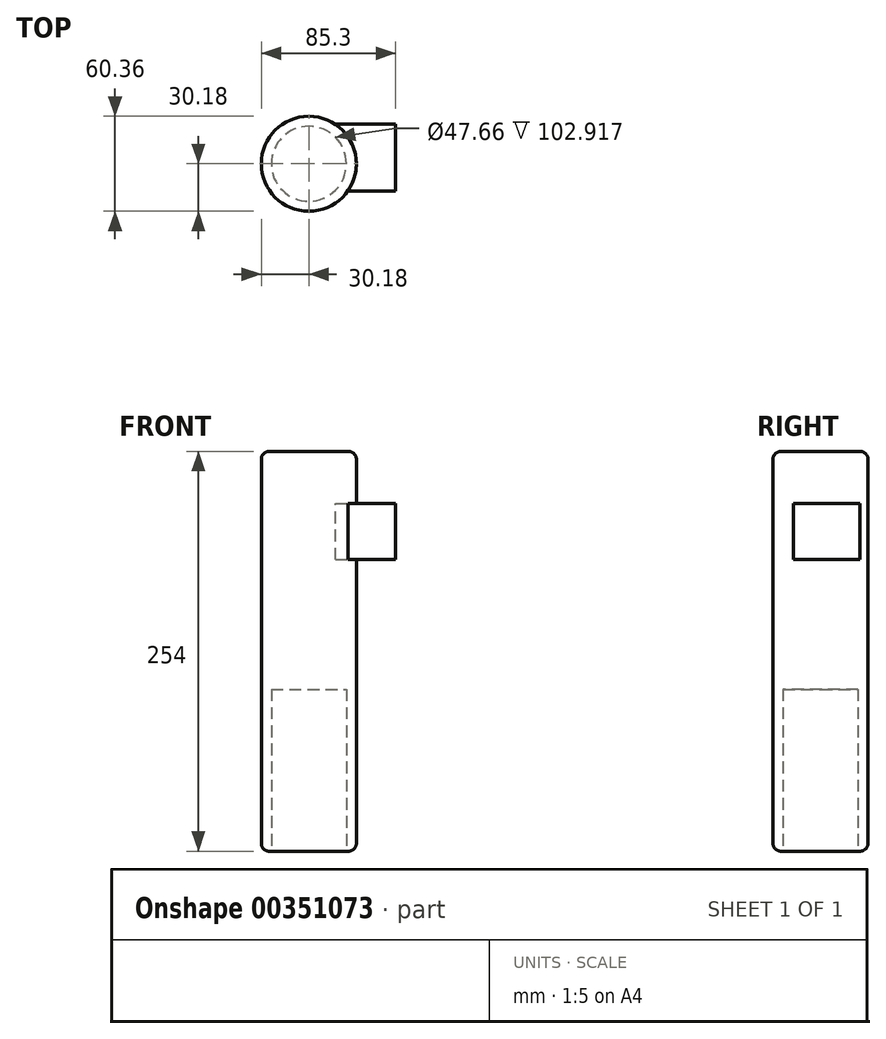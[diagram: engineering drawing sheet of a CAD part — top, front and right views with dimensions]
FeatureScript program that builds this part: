
annotation { "Feature Type Name" : "Feature", "Feature Type Description" : "" }
export const myFeature = defineFeature(function(context is Context, id is Id, definition is map)
    precondition{}
    {
        {
            var Q0;
            Q0=qCreatedBy(makeId("Top.planeOp"),FACE);
            var sketch = newSketch(context, id + "F0", { "sketchPlane" : qUnion([Q0])});
            skCircle(sketch, "E0", {"center": v(0, 0) * mm, "radius": 30.18 * mm});
            skSolve(sketch);
        }
        {
            var Q0;
            Q0=makeQuery(id+"F0.imprint","IMPRINT",FACE,{"disambiguationData":[TD([[makeQuery(id+"F0.imprint","IMPRINT",EDGE,{"derivedFrom":sQuery(id+"F0.wireOp",EDGE,"E0")}),1.0]])]});
            extrude(context, id + "F1", {"entities" : qUnion([Q0]), "oppositeDirection" : true, "depth" : 254 * mm});
        }
        {
            var Q0;
            Q0=makeQuery(id+"F1.opExtrude","CAP_FACE",FACE,{"disambiguationData":[OSD([sQuery(id+"F0.wireOp",EDGE,"E0")])],"isStart":false});
            var sketch = newSketch(context, id + "F2", { "sketchPlane" : qUnion([Q0])});
            skCircle(sketch, "E1.0", {"center": v(0, 0) * mm, "radius": 23.83 * mm});
            skSolve(sketch);
        }
        {
            var Q0;
            Q0=makeQuery(id+"F2.imprint","IMPRINT",FACE,{"disambiguationData":[TD([[makeQuery(id+"F2.imprint","IMPRINT",EDGE,{"derivedFrom":sQuery(id+"F2.wireOp",EDGE,"E1.0")}),1.0]])]});
            extrude(context, id + "F3", {"entities" : qUnion([Q0]), "operationType" : NewBodyOperationType.REMOVE, "oppositeDirection" : true, "depth" : 102.92 * mm});
        }
        {
            var Q0;
            Q0=makeQuery(id+"F1.opExtrude","SWEPT_FACE",FACE,{"disambiguationData":[OSD([sQuery(id+"F0.wireOp",EDGE,"E0")])]});
            var Q1;
            Q1=makeQuery(id+"F1.opExtrude","CAP_EDGE",EDGE,{"disambiguationData":[OSD([sQuery(id+"F0.wireOp",EDGE,"E0")])],"isStart":false});
            fillet(context, id + "F4", {"entities" : qUnion([Q0, Q1]), "radius" : 5.08 * mm, "tangentPropagation" : true, "allowEdgeOverflow" : false});
        }
        {
            var Q0;
            Q0=qCreatedBy(makeId("Right.planeOp"),FACE);
            cPlane(context, id + "F5", {"entities" : qUnion([Q0]), "cplaneType" : CPlaneType.OFFSET, "offset" : 55.12 * mm, "width" : 150 * mm, "height" : 150 * mm});
        }
        {
            var Q0;
            Q0=qCreatedBy(id+"F5.planeOp",FACE);
            var sketch = newSketch(context, id + "F6", { "sketchPlane" : qUnion([Q0])});
            skLineSegment(sketch, "E2.bottom", {"start": v(-17.26, -33) * mm, "end": v(25.08, -33) * mm});
            skLineSegment(sketch, "E2.top", {"start": v(-17.26, -68.7) * mm, "end": v(25.08, -68.7) * mm});
            skLineSegment(sketch, "E2.left", {"start": v(-17.26, -33) * mm, "end": v(-17.26, -68.7) * mm});
            skLineSegment(sketch, "E2.right", {"start": v(25.08, -33) * mm, "end": v(25.08, -68.7) * mm});
            skSolve(sketch);
        }
        {
            var Q0;
            Q0=makeQuery(id+"F6.imprint","IMPRINT",FACE,{"disambiguationData":[TD([[makeQuery(id+"F6.imprint","IMPRINT",EDGE,{"derivedFrom":sQuery(id+"F6.wireOp",EDGE,"E2.bottom")}),-1.0]])]});
            extrude(context, id + "F7", {"entities" : qUnion([Q0]), "operationType" : NewBodyOperationType.ADD, "oppositeDirection" : true, "depth" : 45.83 * mm});
        }
    });
